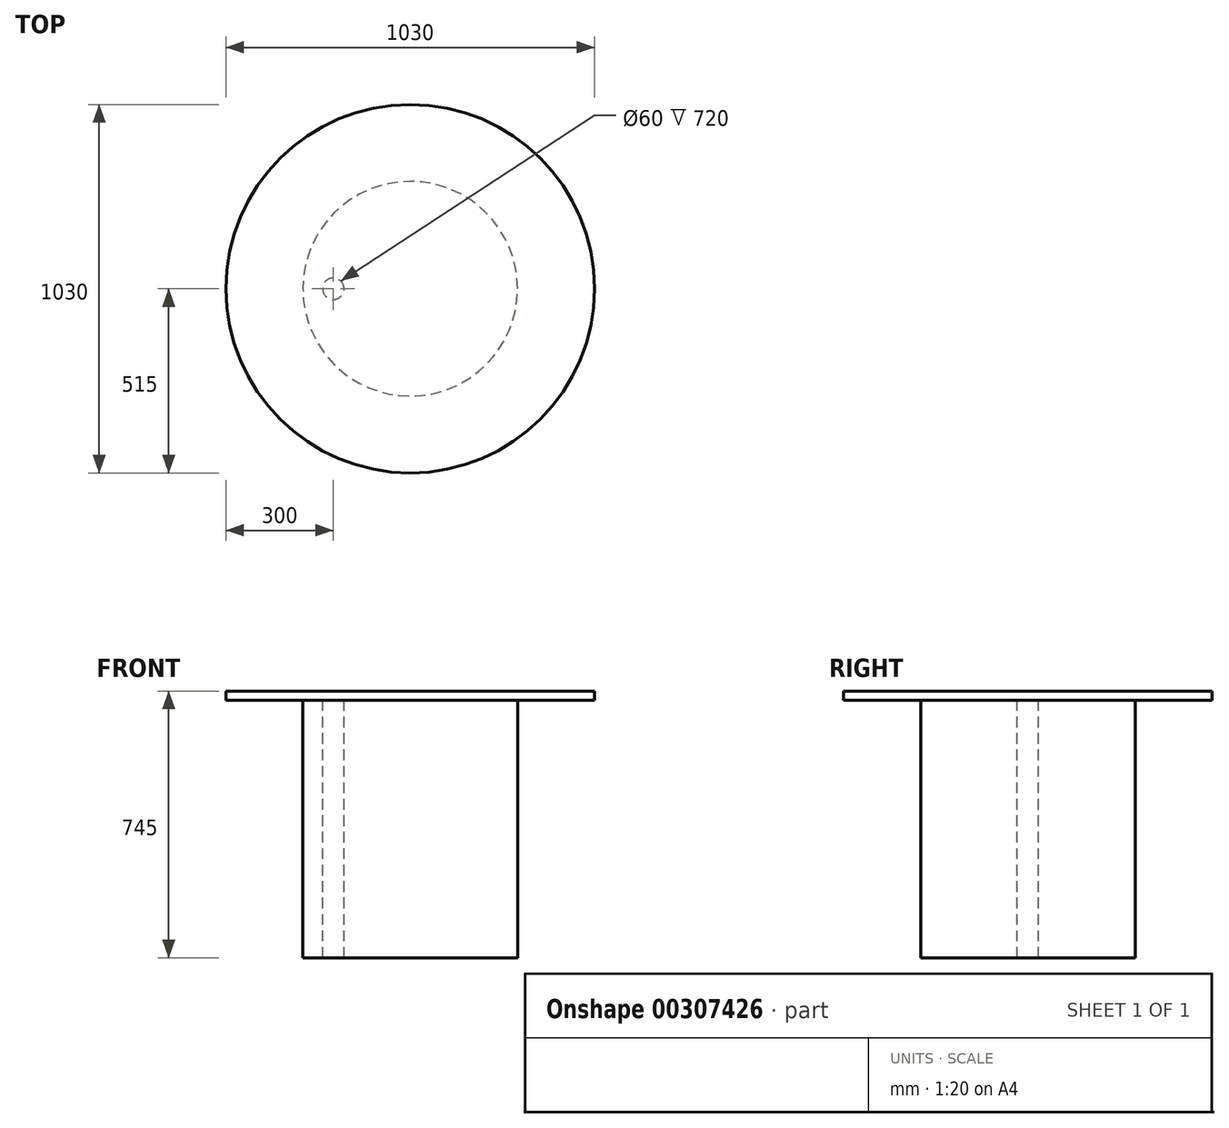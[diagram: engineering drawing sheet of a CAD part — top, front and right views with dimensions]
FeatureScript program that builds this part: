
annotation { "Feature Type Name" : "Feature", "Feature Type Description" : "" }
export const myFeature = defineFeature(function(context is Context, id is Id, definition is map)
    precondition{}
    {
        {
            var Q0;
            Q0=qCreatedBy(makeId("Top.planeOp"),FACE);
            var sketch = newSketch(context, id + "F0", { "sketchPlane" : qUnion([Q0])});
            skCircle(sketch, "E0", {"center": v(0, 0) * mm, "radius": 300 * mm});
            skCircle(sketch, "E1", {"center": v(0, 0) * mm, "radius": 515 * mm});
            skLineSegment(sketch, "E2", {"start": v(-300, 0) * mm, "end": v(300, 0) * mm, "construction": true});
            skLineSegment(sketch, "E3", {"start": v(0, 300) * mm, "end": v(0, -300) * mm, "construction": true});
            skCircle(sketch, "E4", {"center": v(215, 0) * mm, "radius": 30 * mm});
            skLineSegment(sketch, "E5.bottom", {"start": v(10, 85) * mm, "end": v(-10, 85) * mm});
            skLineSegment(sketch, "E5.top", {"start": v(10, 245) * mm, "end": v(-10, 245) * mm});
            skLineSegment(sketch, "E5.left", {"start": v(10, 85) * mm, "end": v(10, 245) * mm});
            skLineSegment(sketch, "E5.right", {"start": v(-10, 85) * mm, "end": v(-10, 245) * mm});
            skPoint(sketch, "E5.middle", {"position": v(0, 165) * mm});
            skPoint(sketch, "E6", {"position": v(245, 0) * mm});
            skCircle(sketch, "E7.MirrorC", {"center": v(-215, 0) * mm, "radius": 30 * mm});
            skLineSegment(sketch, "E8.MirrorCS", {"start": v(-10, -85) * mm, "end": v(-10, -245) * mm});
            skLineSegment(sketch, "E9.MirrorCS", {"start": v(10, -85) * mm, "end": v(10, -245) * mm});
            skLineSegment(sketch, "E10.MirrorCS", {"start": v(10, -85) * mm, "end": v(-10, -85) * mm});
            skLineSegment(sketch, "E11.MirrorCS", {"start": v(10, -245) * mm, "end": v(-10, -245) * mm});
            skSolve(sketch);
        }
        {
            var Q0;
            Q0=makeQuery(id+"F0.imprint","IMPRINT",FACE,{"disambiguationData":[TD([[makeQuery(id+"F0.imprint","IMPRINT",EDGE,{"derivedFrom":sQuery(id+"F0.wireOp",EDGE,"E4")}),1.0]])]});
            var Q1;
            Q1=makeQuery(id+"F0.imprint","IMPRINT",FACE,{"disambiguationData":[TD([[makeQuery(id+"F0.imprint","IMPRINT",EDGE,{"derivedFrom":sQuery(id+"F0.wireOp",EDGE,"E7.MirrorC")}),-1.0]])]});
            var Q2;
            Q2=makeQuery(id+"F0.imprint","IMPRINT",FACE,{"disambiguationData":[TD([[makeQuery(id+"F0.imprint","IMPRINT",EDGE,{"derivedFrom":sQuery(id+"F0.wireOp",EDGE,"E8.MirrorCS")}),1.0]])]});
            var Q3;
            Q3=makeQuery(id+"F0.imprint","IMPRINT",FACE,{"disambiguationData":[TD([[makeQuery(id+"F0.imprint","IMPRINT",EDGE,{"derivedFrom":sQuery(id+"F0.wireOp",EDGE,"E5.bottom")}),-1.0]])]});
            var Q4;
            Q4=makeQuery(id+"F0.imprint","IMPRINT",FACE,{"disambiguationData":[TD([[makeQuery(id+"F0.imprint","IMPRINT",EDGE,{"derivedFrom":sQuery(id+"F0.wireOp",EDGE,"E0")}),1.0]])]});
            extrude(context, id + "F1", {"entities" : qUnion([Q0, Q1, Q2, Q3, Q4]), "oppositeDirection" : true, "depth" : 20 * mm, "offsetDistance" : 25 * mm});
        }
        {
            var Q0;
            Q0=makeQuery(id+"F0.imprint","IMPRINT",FACE,{"disambiguationData":[TD([[makeQuery(id+"F0.imprint","IMPRINT",EDGE,{"derivedFrom":sQuery(id+"F0.wireOp",EDGE,"E4")}),1.0]])]});
            var Q1;
            Q1=makeQuery(id+"F0.imprint","IMPRINT",FACE,{"disambiguationData":[TD([[makeQuery(id+"F0.imprint","IMPRINT",EDGE,{"derivedFrom":sQuery(id+"F0.wireOp",EDGE,"E7.MirrorC")}),-1.0]])]});
            var Q2;
            Q2=makeQuery(id+"F0.imprint","IMPRINT",FACE,{"disambiguationData":[TD([[makeQuery(id+"F0.imprint","IMPRINT",EDGE,{"derivedFrom":sQuery(id+"F0.wireOp",EDGE,"E8.MirrorCS")}),1.0]])]});
            var Q3;
            Q3=makeQuery(id+"F0.imprint","IMPRINT",FACE,{"disambiguationData":[TD([[makeQuery(id+"F0.imprint","IMPRINT",EDGE,{"derivedFrom":sQuery(id+"F0.wireOp",EDGE,"E5.bottom")}),-1.0]])]});
            extrude(context, id + "F2", {"entities" : qUnion([Q0, Q1, Q2, Q3]), "operationType" : NewBodyOperationType.ADD, "depth" : 700 * mm, "offsetDistance" : 25 * mm});
        }
        {
            var Q0;
            Q0=makeQuery(id+"F2.opExtrude","CAP_FACE",FACE,{"disambiguationData":[OSD([sQuery(id+"F0.wireOp",EDGE,"E7.MirrorC")])],"isStart":false});
            var sketch = newSketch(context, id + "F3", { "sketchPlane" : qUnion([Q0])});
            skCircle(sketch, "E12.0", {"center": v(0, 0) * mm, "radius": 515 * mm});
            skSolve(sketch);
        }
        {
            var Q0;
            Q0 = qSketchRegion(id + "F3", true);
            extrude(context, id + "F4", {"entities" : qUnion([Q0]), "operationType" : NewBodyOperationType.ADD, "depth" : 25 * mm, "offsetDistance" : 25 * mm});
        }
    });
